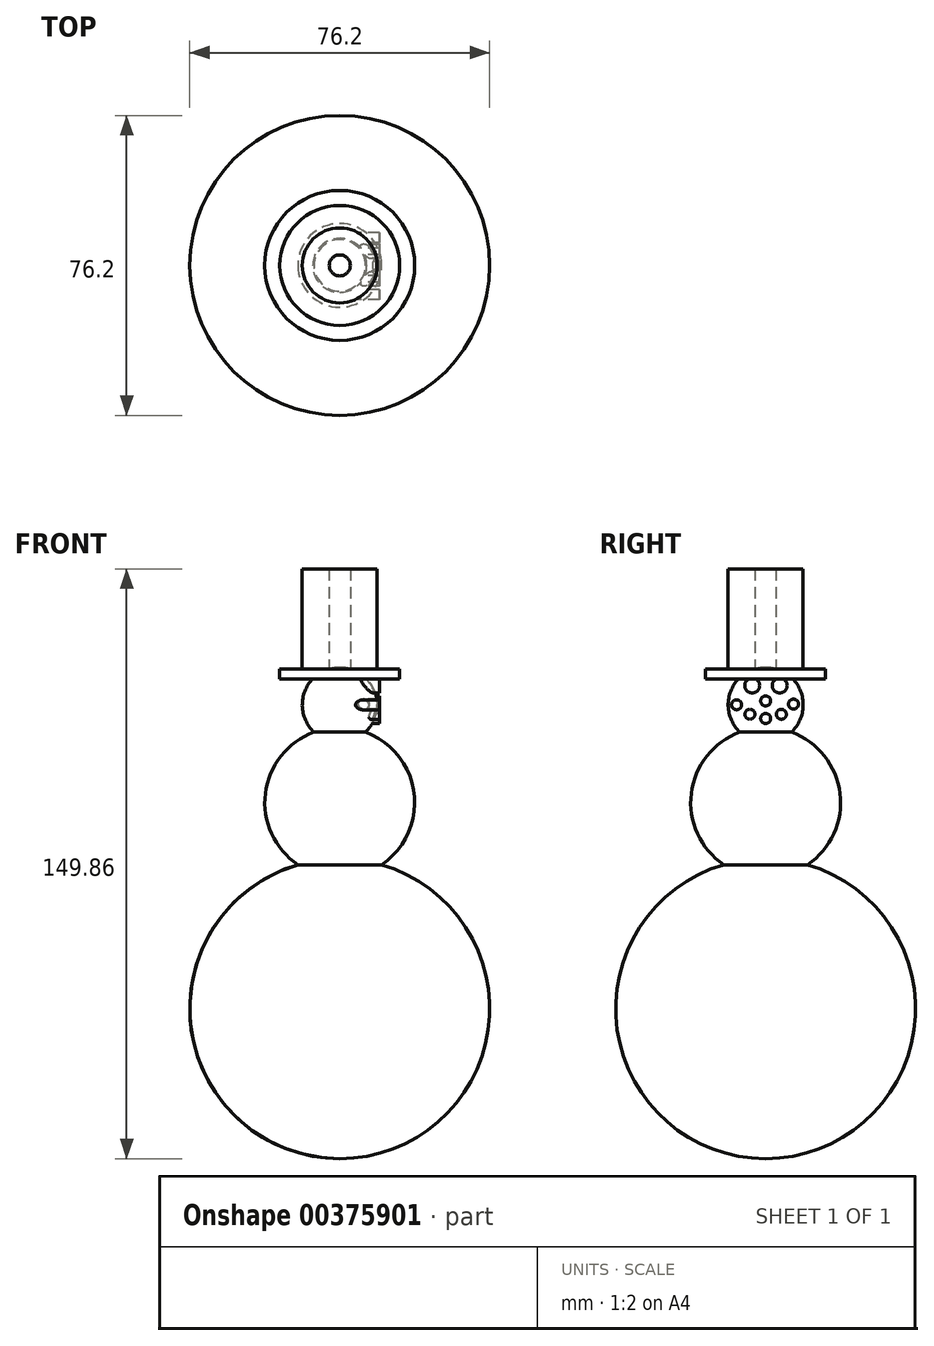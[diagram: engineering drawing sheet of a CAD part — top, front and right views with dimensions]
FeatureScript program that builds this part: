
annotation { "Feature Type Name" : "Feature", "Feature Type Description" : "" }
export const myFeature = defineFeature(function(context is Context, id is Id, definition is map)
    precondition{}
    {
        {
            var Q0;
            Q0=qCreatedBy(makeId("Front.planeOp"),FACE);
            var sketch = newSketch(context, id + "F0", { "sketchPlane" : qUnion([Q0])});
            skArc(sketch, "E0", {"start": v(0, 38.1) * mm, "mid": v(-38.1, 0) * mm, "end": v(0, -38.1) * mm});
            skLineSegment(sketch, "E1", {"start": v(0, 95.25) * mm, "end": v(0, -38.1) * mm, "construction": true});
            skLineSegment(sketch, "E2", {"start": v(0, 95.25) * mm, "end": v(0, -38.1) * mm});
            skArc(sketch, "E3", {"start": v(0, 71.44) * mm, "mid": v(-19.05, 52.39) * mm, "end": v(0, 33.34) * mm});
            skArc(sketch, "E4", {"start": v(0, 86.74) * mm, "mid": v(-9.53, 77.22) * mm, "end": v(0, 67.7) * mm});
            skSolve(sketch);
        }
        {
            var Q0;
            Q0 = qSketchRegion(id + "F0", true);
            var Q1;
            Q1=sQuery(id+"F0.wireOp",EDGE,"E2");
            revolve(context, id + "F1", {"entities" : qUnion([Q0]), "axis" : qUnion([Q1]), "revolveType" : RevolveType.FULL});
        }
        {
            var Q0;
            Q0=qCreatedBy(makeId("Right.planeOp"),FACE);
            var Q1;
            Q1 = qBodyType(qCreatedBy(id + "F3" ,EDGE), BodyType.WIRE);
            cPlane(context, id + "F2", {"entities" : qUnion([Q0, Q1]), "cplaneType" : CPlaneType.OFFSET, "offset" : 0 * mm, "width" : 152.4 * mm, "height" : 152.4 * mm});
        }
        {
            var Q0;
            Q0=qCreatedBy(id+"F2.planeOp",FACE);
            var sketch = newSketch(context, id + "F3", { "sketchPlane" : qUnion([Q0])});
            skLineSegment(sketch, "E5", {"start": v(0, 87.74) * mm, "end": v(0, 59.74) * mm});
            skLineSegment(sketch, "E6", {"start": v(-9.13, 82.13) * mm, "end": v(11.16, 82.13) * mm});
            skCircle(sketch, "E7", {"center": v(-3.42, 82.13) * mm, "radius": 1.9 * mm});
            skCircle(sketch, "E8", {"center": v(3.57, 82.13) * mm, "radius": 1.9 * mm});
            skCircle(sketch, "E9", {"center": v(0, 73.74) * mm, "radius": 1.27 * mm});
            skCircle(sketch, "E10", {"center": v(-7.39, 77.22) * mm, "radius": 1.27 * mm});
            skCircle(sketch, "E11", {"center": v(-4, 74.81) * mm, "radius": 1.27 * mm});
            skCircle(sketch, "E12", {"center": v(7.06, 77.38) * mm, "radius": 1.27 * mm});
            skPoint(sketch, "E13.centerSnap0", {"position": v(0, 78.2) * mm});
            skCircle(sketch, "E14", {"center": v(3.98, 74.8) * mm, "radius": 1.27 * mm});
            skCircle(sketch, "E15", {"center": v(0, 78.2) * mm, "radius": 1.27 * mm});
            skSolve(sketch);
        }
        {
            var Q0;
            Q0 = qSketchRegion(id + "F3", true);
            extrude(context, id + "F4", {"entities" : qUnion([Q0]), "operationType" : NewBodyOperationType.ADD, "depth" : 10.16 * mm});
        }
        {
            var Q0;
            Q0=qCreatedBy(makeId("Top.planeOp"),FACE);
            cPlane(context, id + "F5", {"entities" : qUnion([Q0]), "cplaneType" : CPlaneType.OFFSET, "offset" : 83.82 * mm, "width" : 152.4 * mm, "height" : 152.4 * mm});
        }
        {
            var Q0;
            Q0=qCreatedBy(id+"F5.planeOp",FACE);
            var sketch = newSketch(context, id + "F6", { "sketchPlane" : qUnion([Q0])});
            skCircle(sketch, "E16", {"center": v(0, 0) * mm, "radius": 15.24 * mm});
            skSolve(sketch);
        }
        {
            var Q0;
            Q0=makeQuery(id+"F6.imprint","IMPRINT",FACE,{"disambiguationData":[TD([[makeQuery(id+"F6.imprint","IMPRINT",EDGE,{"derivedFrom":sQuery(id+"F6.wireOp",EDGE,"E16")}),1.0]])]});
            extrude(context, id + "F7", {"entities" : qUnion([Q0]), "operationType" : NewBodyOperationType.ADD, "depth" : 2.54 * mm});
        }
        {
            var Q0;
            Q0=makeQuery(id+"F7.opExtrude","CAP_FACE",FACE,{"disambiguationData":[OSD([sQuery(id+"F6.wireOp",EDGE,"E16")])],"isStart":false});
            var sketch = newSketch(context, id + "F8", { "sketchPlane" : qUnion([Q0])});
            skCircle(sketch, "E17", {"center": v(0, 0) * mm, "radius": 9.53 * mm});
            skSolve(sketch);
        }
        {
            var Q0;
            Q0=makeQuery(id+"F8.imprint","IMPRINT",FACE,{"disambiguationData":[TD([[makeQuery(id+"F8.imprint","IMPRINT",EDGE,{"derivedFrom":sQuery(id+"F8.wireOp",EDGE,"E17")}),1.0]])]});
            extrude(context, id + "F9", {"entities" : qUnion([Q0]), "operationType" : NewBodyOperationType.ADD, "depth" : 25.4 * mm});
        }
    });
